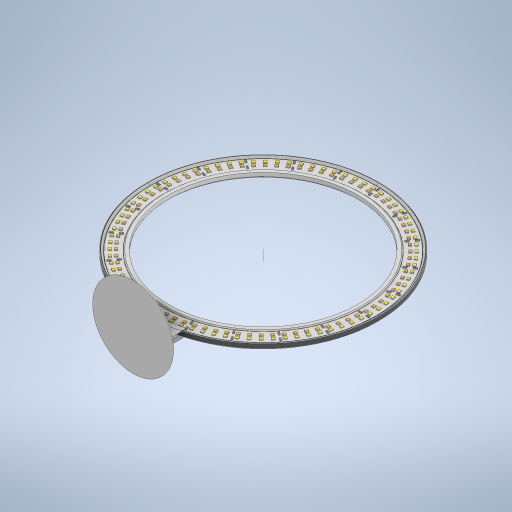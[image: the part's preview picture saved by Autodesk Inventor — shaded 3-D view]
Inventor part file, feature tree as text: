
AUTODESK INVENTOR PART (.ipt)
format: ipt  version: 2024.1 (Build 281209000, 209)  size: 3,021,824 bytes
history: native  units: mm
features: sketch x13, extrude x13, other x9, projected_geometry x9, chamfer x5, pattern_circular x3, fillet x3
ambient origin geometry x8: Origin, YZ Plane, XZ Plane, XY Plane, X Axis, Y Axis, Z Axis, Center Point
bodies: Solid7 (feature_tree), Solid8 (feature_tree), Solid9 (feature_tree)
feature tree (55):
  other  "led-ring"
  sketch  "Sketch1"  dims[d0=221.0mm d1=15.0mm]
  extrude  "Extrusion1"  Depth=15.0mm
  extrude  "Extrusion2"  Depth=2.8mm
  other  "Work Axis1"
  pattern_circular  "Circular Pattern1"  Count=80 Angle=360.0deg
  extrude  "Extrusion3"  Depth=1.6mm
  pattern_circular  "Circular Pattern2"  Count=20 Angle=360.0deg
  extrude  "Extrusion4"  Depth=3.0mm
  chamfer  "Chamfer3"  Distance=0.3mm
  extrude  "Extrusion5"  Depth=3.0mm TaperAngle=0.0deg
  extrude  "Extrusion6"  Depth=3.0mm
  extrude  "Extrusion12"  Depth=3.0mm
  chamfer  "Chamfer4"  Distance=2.0mm
  chamfer  "Chamfer5"  Distance=0.4mm
  pattern_circular  "Circular Pattern3"  [2 undecoded]
  extrude  "Extrusion7"  Depth=3.0mm
  extrude  "Extrusion8"  Depth=3.0mm
  extrude  "Extrusion9"  Depth=3.0mm
  fillet  "Fillet2"  Radius=4.0mm
  fillet  "Fillet3"  Radius=2.25mm
  extrude  "Extrusion10"  Depth=10.0mm TaperAngle=0.0deg
  fillet  "Fillet4"  Radius=80.0mm
  extrude  "Extrusion11"  Depth=3.0mm
  chamfer  "Chamfer6"  Distance=90.0mm
  chamfer  "Chamfer7"  Distance=5.0mm
  extrude  "Extrusion13"  Depth=3.0mm
  sketch  "Sketch2"  dims[d2=1.06mm d3=0.0mm d4=2.8mm]
  projected_geometry  "Projected Loop1"
  sketch  "Sketch3"  dims[d5=3.2mm]
  projected_geometry  "Projected Loop2"
  sketch  "Sketch5"  dims[d6=2.8mm]
  other  "inside-ring-mount"
  sketch  "Sketch6"  dims[d7=3.2mm]
  projected_geometry  "Projected Loop3"
  sketch  "Sketch7"  dims[d8=2.22mm]
  sketch  "Sketch8"  dims[d9=0.9mm d10=0.0mm d11=800.0mm d12=360.0deg]
  sketch  "Sketch9"  dims[d14=1.6mm d15=1.44mm]
  projected_geometry  "Projected Loop4"
  sketch  "Sketch10"  dims[d16=3.6mm]
  other  "RING-STAND"
  projected_geometry  "Projected Loop6"
  sketch  "Sketch12"  dims[d17=3.6mm]
  projected_geometry  "Projected Loop7"
  other  "foot"
  sketch  "Sketch13"  dims[d18=1.53mm]
  projected_geometry  "Projected Loop8"
  other  "outside-ring-mount"
  sketch  "Sketch15"  dims[d19=1.53mm]
  projected_geometry  "Projected Loop9"
  projected_geometry  "Projected Loop10"
  other  "Pattern of outside-ring-mount:1"
  other  "Pattern of outside-ring-mount:2"
  other  "Pattern of outside-ring-mount:3"
  sketch  "Sketch16"  dims[d20=0.7mm d21=0.0mm d22=200.0mm d23=360.0deg d25=5.0mm d26=0.3mm d27=2.1mm d28=0.0mm d29=3.0mm d30=3.0mm d31=2.0mm d32=0.0mm d33=0.4mm d34=5.0mm d35=0.0mm d42=30.0mm d43=30.0mm d44=15.0mm d45=4.0mm d46=9.0mm d47=0.0mm d48=0.0mm d49=2.25mm d50=0.0mm d51=10.0mm d52=0.0mm d55=80.0mm d56=15.0mm d57=90.0mm d58=5.0mm d59=0.0mm d60=13.0mm d61=5.0mm d62=0.0mm d63=1.0mm d64=2.0mm d65=45.0deg d66=3.0mm d67=2.0mm d68=0.0mm d69=2.0mm d70=2.0mm d71=45.0deg d72=0.5mm d73=2.0mm d74=45.0deg d75=40.0mm d76=360.0deg d78=2.0mm d79=2.0mm d80=45.0deg d81=2.0mm d82=2.0mm d83=45.0deg d84=3.0mm d85=5.0mm d86=3.0mm d87=0.0mm d88=0.0mm]
note: 2 required parameter values undecoded (feature->parameter linkage not recoverable at this tier; creation-order binding heuristic only, values carry confidence <= 0.55)
